FCSTD DOCUMENT  (FreeCAD 0.15R4671 (Git))
Label: YCarrageBottom_II
License: All rights reserved
LicenseURL: http://en.wikipedia.org/wiki/All_rights_reserved
objects: Sketcher::SketchObject×21, PartDesign::Pocket×17, Mesh::Feature×15, Part::Feature×8, PartDesign::Fillet×5, PartDesign::Pad×4, PartDesign::Chamfer×2
note: 78 computed .brp shape members not serialized (recipe doc carries the construction recipe); baked Part::Feature solids carry a one-line shape summary decoded from their .brp

FEATURE [Part::Feature] Part__Feature  label="YCarrage"
  shape: bbox 35 x 59 x 36 mm, 127 faces (baked)
FEATURE [Sketcher::SketchObject] Sketch
  Placement = pos=(0,0,-14) rot=(0,0,1;0rad)
  sketch-geometry (4):
    g0: LineSegment StartX=60 StartY=17 StartZ=0 EndX=22 EndY=17 EndZ=0
    g1: LineSegment StartX=22 StartY=17 StartZ=0 EndX=22 EndY=-42 EndZ=0
    g2: LineSegment StartX=22 StartY=-42 StartZ=0 EndX=60 EndY=-42 EndZ=0
    g3: LineSegment StartX=60 StartY=-42 StartZ=0 EndX=60 EndY=17 EndZ=0
  constraints (8):
    c: Coincident(g0,g1)
    c: Coincident(g1,g2)
    c: Coincident(g2,g3)
    c: Coincident(g3,g0)
    c: Horizontal(g0)
    c: Horizontal(g2)
    c: Vertical(g1)
    c: Vertical(g3)
FEATURE [PartDesign::Pad] Pad
  Length = 36
  Length2 = 100
  Placement = pos=(0,0,-14) rot=(0,0,1;0rad)
  Sketch = -> Sketch
  Type = 0
FEATURE [Sketcher::SketchObject] Sketch001
  Placement = pos=(0,0,22) rot=(0,0,1;0rad)
  Support = -> Pad [Face6]
  sketch-geometry (10):
    g0: LineSegment StartX=62 StartY=17 StartZ=0 EndX=58 EndY=17 EndZ=0
    g1: LineSegment StartX=58 StartY=17 StartZ=0 EndX=45 EndY=6 EndZ=0
    g2: LineSegment StartX=45 StartY=6 StartZ=0 EndX=45 EndY=-31 EndZ=0
    g3: LineSegment StartX=45 StartY=-31 StartZ=0 EndX=58 EndY=-42 EndZ=0
    g4: LineSegment StartX=58 StartY=-42 StartZ=0 EndX=61 EndY=-42 EndZ=0
    g5: LineSegment StartX=61 StartY=-42 StartZ=0 EndX=61 EndY=-44 EndZ=0
    g6: LineSegment StartX=61 StartY=-44 StartZ=0 EndX=20 EndY=-44 EndZ=0
    g7: LineSegment StartX=20 StartY=-44 StartZ=0 EndX=20 EndY=19 EndZ=0
    g8: LineSegment StartX=20 StartY=19 StartZ=0 EndX=62 EndY=19 EndZ=0
    g9: LineSegment StartX=62 StartY=19 StartZ=0 EndX=62 EndY=17 EndZ=0
  constraints (18):
    c: Horizontal(g0)
    c: Coincident(g0,g1)
    c: Coincident(g1,g2)
    c: Vertical(g2)
    c: Coincident(g2,g3)
    c: Coincident(g3,g4)
    c: Horizontal(g4)
    c: Coincident(g4,g5)
    c: Vertical(g5)
    c: Coincident(g5,g6)
    c: Horizontal(g6)
    c: Coincident(g6,g7)
    c: Vertical(g7)
    c: Coincident(g7,g8)
    c: Horizontal(g8)
    c: Coincident(g8,g9)
    c: Vertical(g9)
    c: Coincident(g0,g9)
FEATURE [PartDesign::Pocket] Pocket
  Length = 13
  Placement = pos=(0,0,-14) rot=(0,0,1;0rad)
  Sketch = -> Sketch001
  Type = 0
FEATURE [Sketcher::SketchObject] Sketch002
  Placement = pos=(0,-42,-14) rot=(1,0,0;1.5708rad)
  Support = -> Pocket [Face10]
  sketch-geometry (1):
    g0: Circle CenterX=36 CenterY=10.5 CenterZ=0 NormalX=0 NormalY=0 NormalZ=1 Radius=7.75
  constraints (1):
    c: Radius(g0) = 7.75
FEATURE [PartDesign::Pocket] Pocket001
  Length = 26.75
  Placement = pos=(0,0,-14) rot=(0,0,1;0rad)
  Sketch = -> Sketch002
  Type = 0
FEATURE [Sketcher::SketchObject] Sketch003
  Placement = pos=(0,17,-14) rot=(0,0.707107,0.707107;3.14159rad)
  Support = -> Pocket001 [Face2]
  sketch-geometry (1):
    g0: Circle CenterX=-36 CenterY=10.5 CenterZ=0 NormalX=0 NormalY=0 NormalZ=1 Radius=7.75
  constraints (1):
    c: Radius(g0) = 7.75
FEATURE [PartDesign::Pocket] Pocket002
  Length = 26.75
  Placement = pos=(0,0,-14) rot=(0,0,1;0rad)
  Sketch = -> Sketch003
  Type = 0
FEATURE [Sketcher::SketchObject] Sketch004
  Placement = pos=(0,-42,-14) rot=(1,0,0;1.5708rad)
  Support = -> Pocket002 [Face4]
  sketch-geometry (4):
    g0: LineSegment StartX=28 StartY=18.5 StartZ=0 EndX=44.5 EndY=18.5 EndZ=0
    g1: LineSegment StartX=44.5 StartY=18.5 StartZ=0 EndX=44.5 EndY=2.5 EndZ=0
    g2: LineSegment StartX=44.5 StartY=2.5 StartZ=0 EndX=28 EndY=2.5 EndZ=0
    g3: LineSegment StartX=28 StartY=2.5 StartZ=0 EndX=28 EndY=18.5 EndZ=0
  constraints (8):
    c: Coincident(g0,g1)
    c: Coincident(g1,g2)
    c: Coincident(g2,g3)
    c: Coincident(g3,g0)
    c: Horizontal(g0)
    c: Horizontal(g2)
    c: Vertical(g1)
    c: Vertical(g3)
FEATURE [PartDesign::Pad] Pad001
  Length = 1.25
  Length2 = 100
  Placement = pos=(0,0,-14) rot=(0,0,1;0rad)
  Reversed = true
  Sketch = -> Sketch004
  Type = 0
FEATURE [Sketcher::SketchObject] Sketch005
  Placement = pos=(0,17,-14) rot=(0,0.707107,0.707107;3.14159rad)
  Support = -> Pad001 [Face2]
  sketch-geometry (4):
    g0: LineSegment StartX=-44.6266 StartY=19 StartZ=0 EndX=-27.8702 EndY=19 EndZ=0
    g1: LineSegment StartX=-27.8702 StartY=19 StartZ=0 EndX=-27.8702 EndY=2.37723 EndZ=0
    g2: LineSegment StartX=-27.8702 StartY=2.37723 StartZ=0 EndX=-44.6266 EndY=2.37723 EndZ=0
    g3: LineSegment StartX=-44.6266 StartY=2.37723 StartZ=0 EndX=-44.6266 EndY=19 EndZ=0
  constraints (8):
    c: Coincident(g0,g1)
    c: Coincident(g1,g2)
    c: Coincident(g2,g3)
    c: Coincident(g3,g0)
    c: Horizontal(g0)
    c: Horizontal(g2)
    c: Vertical(g1)
    c: Vertical(g3)
FEATURE [PartDesign::Pad] Pad002
  Length = 1.25
  Length2 = 100
  Placement = pos=(0,0,-14) rot=(0,0,1;0rad)
  Reversed = true
  Sketch = -> Sketch005
  Type = 0
FEATURE [Part::Feature] Pad002001  label="Pad003"
  shape: bbox 38 x 59 x 36 mm, 16 faces (baked)
FEATURE [Sketcher::SketchObject] Sketch006
  Placement = pos=(0,17,0) rot=(0,0.707107,0.707107;3.14159rad)
  Support = -> Pad002001 [Face10]
  sketch-geometry (1):
    g0: Circle CenterX=-36 CenterY=-3.5 CenterZ=0 NormalX=0 NormalY=0 NormalZ=1 Radius=6
  constraints (1):
    c: Radius(g0) = 6
FEATURE [PartDesign::Pocket] Pocket003
  Length = 5
  Sketch = -> Sketch006
  Type = 1
FEATURE [Mesh::Feature] _mmRod_x100mm  label="8mmRod_x100mm001"
  Placement = pos=(45,7.5,1.5) rot=(0,0,1;1.5708rad)
FEATURE [Mesh::Feature] _mmRod_x100mm001  label="8mmRod_x100mm002"
  Placement = pos=(45,-32.5,1.5) rot=(0,0,1;1.5708rad)
FEATURE [Part::Feature] Part__Feature001  label="T5_Pulley"
  Placement = pos=(36,176,-4) rot=(0,0,1;0rad)
  shape: bbox 16 x 16 x 14.8 mm, 116 faces (baked)
FEATURE [Part::Feature] Part__Feature002  label="NEMA17"
  Placement = pos=(36,176,2) rot=(0,0,1;0rad)
  shape: bbox 42.3 x 42.3 x 68 mm, 275 faces (baked)
FEATURE [Part::Feature] LM8UU_8mm_Linear_Bearing
  Placement = pos=(36,-9,-3.5) rot=(0,0,1;1.5708rad)
  shape: bbox 15 x 24 x 15 mm, 34 faces (baked)
FEATURE [Mesh::Feature] _x10x4_FlangedBearing  label="5x10x4_FlangedBearing_BOTTOM"
  Placement = pos=(49,-6,16) rot=(-1,0,0;1.5708rad)
FEATURE [Mesh::Feature] _x10x4_FlangedBearing001  label="5x10x4_FlangedBearing_TOP"
  Placement = pos=(49,-6,12) rot=(1,0,0;1.5708rad)
FEATURE [Mesh::Feature] _x10x4_FlangedBearing002  label="5x10x4_FlangedBearing_BOTTOM001"
  Placement = pos=(49,-19,16) rot=(-1,0,0;1.5708rad)
FEATURE [Mesh::Feature] _x10x4_FlangedBearing003  label="5x10x4_FlangedBearing_TOP001"
  Placement = pos=(49,-19,12) rot=(1,0,0;1.5708rad)
FEATURE [Part::Feature] LM8UU_8mm_Linear_Bearing001
  Placement = pos=(36,-40,-3.5) rot=(0,0,1;1.5708rad)
  shape: bbox 15 x 24 x 15 mm, 34 faces (baked)
FEATURE [Mesh::Feature] HexNutStyle1_M002
  Placement = pos=(55.3,-11.85,-128.5) rot=(0,0,1;0.523599rad)
FEATURE [Mesh::Feature] HexNutStyle1_M003
  Placement = pos=(55.3,39.15,-128.5) rot=(0,0,1;0.523599rad)
FEATURE [Mesh::Feature] HexNutStyle1_M004
  Placement = pos=(55.3,13.65,-128.5) rot=(0,0,1;0.523599rad)
FEATURE [Sketcher::SketchObject] Sketch007
  Placement = pos=(45,0,0) rot=(0.57735,-0.57735,-0.57735;2.0944rad)
  Support = -> Pocket003 [Face12]
  sketch-geometry (4):
    g0: LineSegment StartX=-1.75 StartY=18.25 StartZ=0 EndX=26.75 EndY=18.25 EndZ=0
    g1: LineSegment StartX=26.75 StartY=18.25 StartZ=0 EndX=26.75 EndY=9.75 EndZ=0
    g2: LineSegment StartX=26.75 StartY=9.75 StartZ=0 EndX=-1.75 EndY=9.75 EndZ=0
    g3: LineSegment StartX=-1.75 StartY=9.75 StartZ=0 EndX=-1.75 EndY=18.25 EndZ=0
  constraints (8):
    c: Coincident(g0,g1)
    c: Coincident(g1,g2)
    c: Coincident(g2,g3)
    c: Coincident(g3,g0)
    c: Horizontal(g0)
    c: Horizontal(g2)
    c: Vertical(g1)
    c: Vertical(g3)
FEATURE [PartDesign::Pocket] Pocket004
  Length = 11
  Sketch = -> Sketch007
  Type = 0
FEATURE [Sketcher::SketchObject] Sketch008
  Placement = pos=(60,0,0) rot=(0.57735,0.57735,0.57735;2.0944rad)
  Support = -> Pocket004 [Face5]
  sketch-geometry (4):
    g0: LineSegment StartX=-15 StartY=18.25 StartZ=0 EndX=-10 EndY=18.25 EndZ=0
    g1: LineSegment StartX=-10 StartY=18.25 StartZ=0 EndX=-10 EndY=9.75 EndZ=0
    g2: LineSegment StartX=-10 StartY=9.75 StartZ=0 EndX=-15 EndY=9.75 EndZ=0
    g3: LineSegment StartX=-15 StartY=9.75 StartZ=0 EndX=-15 EndY=18.25 EndZ=0
  constraints (8):
    c: Coincident(g0,g1)
    c: Coincident(g1,g2)
    c: Coincident(g2,g3)
    c: Coincident(g3,g0)
    c: Horizontal(g0)
    c: Horizontal(g2)
    c: Vertical(g1)
    c: Vertical(g3)
FEATURE [PartDesign::Pocket] Pocket005
  Length = 5
  Sketch = -> Sketch008
  Type = 1
FEATURE [Sketcher::SketchObject] Sketch009
  Placement = pos=(0,0,22) rot=(0,0,1;0rad)
  Support = -> Pocket005 [Face7]
  sketch-geometry (2):
    g0: Circle CenterX=49 CenterY=-6 CenterZ=0 NormalX=0 NormalY=0 NormalZ=1 Radius=1.8
    g1: Circle CenterX=49 CenterY=-19 CenterZ=0 NormalX=0 NormalY=0 NormalZ=1 Radius=1.8
  constraints (2):
    c: Radius(g1) = 1.8
    c: Equal(g1,g0)
FEATURE [PartDesign::Pocket] Pocket006
  Length = 30
  Sketch = -> Sketch009
  Type = 0
FEATURE [Sketcher::SketchObject] Sketch010
  Placement = pos=(0,0,-14) rot=(1,0,0;3.14159rad)
  Support = -> Pocket006 [Face1]
  sketch-geometry (2):
    g0: Circle CenterX=49 CenterY=19 CenterZ=0 NormalX=0 NormalY=0 NormalZ=1 Radius=1
    g1: Circle CenterX=49 CenterY=6 CenterZ=0 NormalX=0 NormalY=0 NormalZ=1 Radius=1
  constraints (2):
    c: Radius(g0) = 1
    c: Equal(g0,g1)
FEATURE [PartDesign::Pocket] Pocket007
  Length = 5
  Sketch = -> Sketch010
  Type = 1
FEATURE [PartDesign::Chamfer] Chamfer
  Base = -> Pocket007 [Edge65,Edge54]
  Size = 3.5
FEATURE [Mesh::Feature] HexNutStyle1_M
  Placement = pos=(25.3,-1.84,-117) rot=(0,0,1;0.523599rad)
FEATURE [Mesh::Feature] SocketHeadCapScrew_M3x  label="SocketHeadCapScrew_M3x8"
  Placement = pos=(16.1,-18.09,109) rot=(0,1,0;3.14159rad)
FEATURE [Mesh::Feature] HexNutStyle1_M005
  Placement = pos=(25.3,29.16,-117) rot=(0,0,1;0.523599rad)
FEATURE [Mesh::Feature] SocketHeadCapScrew_M3x001  label="SocketHeadCapScrew_M3x009"
  Placement = pos=(16.1,12.91,109) rot=(0,1,0;3.14159rad)
FEATURE [Mesh::Feature] HexNutStyle1_M006
  Placement = pos=(49,14,-117) rot=(0,0,1;0.523599rad)
FEATURE [Mesh::Feature] SocketHeadCapScrew_M3x002  label="SocketHeadCapScrew_M3x010"
  Placement = pos=(39.8,-2.25,109) rot=(0,1,0;3.14159rad)
FEATURE [Sketcher::SketchObject] Sketch012
  Placement = pos=(0,0,9) rot=(0,0,1;0rad)
  Support = -> Chamfer [Face20]
  sketch-geometry (8):
    g0: ArcOfCircle CenterX=24 CenterY=-28 CenterZ=0 NormalX=0 NormalY=0 NormalZ=1 Radius=5 StartAngle=1.5708 EndAngle=4.71239
    g1: LineSegment StartX=24 StartY=-33 StartZ=0 EndX=25 EndY=-33 EndZ=0
    g2: LineSegment StartX=25 StartY=-33 StartZ=0 EndX=25 EndY=-23 EndZ=0
    g3: LineSegment StartX=25 StartY=-23 StartZ=0 EndX=24 EndY=-23 EndZ=0
    g4: ArcOfCircle CenterX=24 CenterY=3 CenterZ=0 NormalX=0 NormalY=0 NormalZ=1 Radius=5 StartAngle=1.5708 EndAngle=4.71239
    g5: LineSegment StartX=24 StartY=-2 StartZ=0 EndX=25 EndY=-2 EndZ=0
    g6: LineSegment StartX=25 StartY=-2 StartZ=0 EndX=25 EndY=8 EndZ=0
    g7: LineSegment StartX=25 StartY=8 StartZ=0 EndX=24 EndY=8 EndZ=0
  constraints (14):
    c: Tangent(g0,g1) = -1.5708
    c: Coincident(g1,g2)
    c: Vertical(g2)
    c: Coincident(g2,g3)
    c: Coincident(g3,g0)
    c: Horizontal(g3)
    c: Radius(g0) = 5
    c: Radius(g4) = 5
    c: Tangent(g4,g5) = -1.5708
    c: Coincident(g5,g6)
    c: Vertical(g6)
    c: Coincident(g6,g7)
    c: Coincident(g7,g4)
    c: Horizontal(g7)
FEATURE [PartDesign::Pad] Pad002002
  Length = 23
  Length2 = 100
  Reversed = true
  Sketch = -> Sketch012
  Type = 0
FEATURE [Sketcher::SketchObject] Sketch013
  Placement = pos=(0,0,9) rot=(0,0,1;0rad)
  Support = -> Pad002002 [Face41]
  sketch-geometry (2):
    g0: Circle CenterX=24 CenterY=3 CenterZ=0 NormalX=0 NormalY=0 NormalZ=1 Radius=1.8
    g1: Circle CenterX=24 CenterY=-28 CenterZ=0 NormalX=0 NormalY=0 NormalZ=1 Radius=1.8
  constraints (2):
    c: Radius(g1) = 1.8
    c: Equal(g1,g0)
FEATURE [PartDesign::Pocket] Pocket008
  Length = 5
  Sketch = -> Sketch013
  Type = 1
FEATURE [Sketcher::SketchObject] Sketch014
  Placement = pos=(0,0,-14) rot=(1,0,0;3.14159rad)
  Support = -> Pocket008 [Face16]
  sketch-geometry (2):
    g0: Circle CenterX=24 CenterY=28 CenterZ=0 NormalX=0 NormalY=0 NormalZ=1 Radius=3.5
    g1: Circle CenterX=24 CenterY=-3 CenterZ=0 NormalX=0 NormalY=0 NormalZ=1 Radius=3.5
  constraints (2):
    c: Radius(g0) = 3.5
    c: Equal(g0,g1)
FEATURE [PartDesign::Pocket] Pocket009
  Length = 8.5
  Sketch = -> Sketch014
  Type = 0
FEATURE [Sketcher::SketchObject] Sketch015
  Placement = pos=(22,0,0) rot=(0.57735,-0.57735,-0.57735;2.0944rad)
  Support = -> Pocket009 [Face28]
  sketch-geometry (8):
    g0: LineSegment StartX=-6 StartY=2.25 StartZ=0 EndX=0 EndY=2.25 EndZ=0
    g1: LineSegment StartX=0 StartY=2.25 StartZ=0 EndX=0 EndY=-0.5 EndZ=0
    g2: LineSegment StartX=0 StartY=-0.5 StartZ=0 EndX=-6 EndY=-0.5 EndZ=0
    g3: LineSegment StartX=-6 StartY=-0.5 StartZ=0 EndX=-6 EndY=2.25 EndZ=0
    g4: LineSegment StartX=25 StartY=2.25 StartZ=0 EndX=31 EndY=2.25 EndZ=0
    g5: LineSegment StartX=31 StartY=2.25 StartZ=0 EndX=31 EndY=-0.5 EndZ=0
    g6: LineSegment StartX=31 StartY=-0.5 StartZ=0 EndX=25 EndY=-0.5 EndZ=0
    g7: LineSegment StartX=25 StartY=-0.5 StartZ=0 EndX=25 EndY=2.25 EndZ=0
  constraints (17):
    c: Coincident(g0,g1)
    c: Coincident(g1,g2)
    c: Coincident(g2,g3)
    c: Coincident(g3,g0)
    c: Horizontal(g0)
    c: Horizontal(g2)
    c: Vertical(g1)
    c: Vertical(g3)
    c: PointOnObject(g1,g-2)
    c: Coincident(g4,g5)
    c: Coincident(g5,g6)
    c: Coincident(g6,g7)
    c: Coincident(g7,g4)
    c: Horizontal(g4)
    c: Horizontal(g6)
    c: Vertical(g5)
    c: Vertical(g7)
FEATURE [PartDesign::Pocket] Pocket010
  Length = 11.5
  Midplane = true
  Sketch = -> Sketch015
  Type = 0
FEATURE [Sketcher::SketchObject] Sketch016
  Placement = pos=(60,0,0) rot=(0.57735,0.57735,0.57735;2.0944rad)
  Support = -> Pocket010 [Face4]
  sketch-geometry (4):
    g0: LineSegment StartX=-15 StartY=2.25 StartZ=0 EndX=-9.25 EndY=2.25 EndZ=0
    g1: LineSegment StartX=-9.25 StartY=2.25 StartZ=0 EndX=-9.25 EndY=-0.5 EndZ=0
    g2: LineSegment StartX=-9.25 StartY=-0.5 StartZ=0 EndX=-15 EndY=-0.5 EndZ=0
    g3: LineSegment StartX=-15 StartY=-0.5 StartZ=0 EndX=-15 EndY=2.25 EndZ=0
  constraints (8):
    c: Coincident(g0,g1)
    c: Coincident(g1,g2)
    c: Coincident(g2,g3)
    c: Coincident(g3,g0)
    c: Horizontal(g0)
    c: Horizontal(g2)
    c: Vertical(g1)
    c: Vertical(g3)
FEATURE [PartDesign::Pocket] Pocket011
  Length = 16
  Sketch = -> Sketch016
  Type = 0
FEATURE [Sketcher::SketchObject] Sketch017
  Placement = pos=(0,0,-14) rot=(1,0,0;3.14159rad)
  Support = -> Pocket011 [Face16]
  sketch-geometry (1):
    g0: Circle CenterX=47.6923 CenterY=12.121 CenterZ=0 NormalX=0 NormalY=0 NormalZ=1 Radius=1.8
  constraints (1):
    c: Radius(g0) = 1.8
FEATURE [PartDesign::Pocket] Pocket012
  Length = 18
  Sketch = -> Sketch017
  Type = 0
FEATURE [Sketcher::SketchObject] Sketch018
  Placement = pos=(0,0,-14) rot=(1,0,0;3.14159rad)
  Support = -> Pocket012 [Face16]
  sketch-geometry (1):
    g0: Circle CenterX=47.6917 CenterY=12.1202 CenterZ=0 NormalX=0 NormalY=0 NormalZ=1 Radius=3.5
  constraints (1):
    c: Radius(g0) = 3.5
FEATURE [PartDesign::Pocket] Pocket013
  Length = 8.5
  Sketch = -> Sketch018
  Type = 0
FEATURE [Sketcher::SketchObject] Sketch019
  Placement = pos=(60,0,0) rot=(0.57735,0.57735,0.57735;2.0944rad)
  Support = -> Pocket013 [Face4]
  sketch-geometry (2):
    g0: Circle CenterX=-32.5 CenterY=1.5 CenterZ=0 NormalX=0 NormalY=0 NormalZ=1 Radius=4.2
    g1: Circle CenterX=7.5 CenterY=1.5 CenterZ=0 NormalX=0 NormalY=0 NormalZ=1 Radius=4.2
  constraints (2):
    c: Radius(g1) = 4.2
    c: Equal(g1,g0)
FEATURE [PartDesign::Pocket] Pocket014
  Length = 15
  Sketch = -> Sketch019
  Type = 0
FEATURE [Part::Feature] Pocket015
  shape: bbox 41 x 59 x 36 mm, 73 faces (baked)
FEATURE [PartDesign::Chamfer] Chamfer001
  Base = -> Pocket015 [Edge76,Edge60]
  Size = 4
FEATURE [PartDesign::Fillet] Fillet
  Base = -> Chamfer001 [Edge59,Edge62,Edge63,Edge64,Edge69,Edge70,Edge23,Edge2]
  Radius = 2
FEATURE [PartDesign::Fillet] Fillet001
  Base = -> Fillet [Edge151,Edge66]
  Radius = 2
FEATURE [PartDesign::Fillet] Fillet002
  Base = -> Fillet001 [Edge53,Edge27]
  Radius = 2
FEATURE [PartDesign::Fillet] Fillet003
  Base = -> Fillet002 [Edge26,Edge96]
  Radius = 1
FEATURE [PartDesign::Fillet] Fillet004
  Base = -> Fillet003 [Edge48]
  Radius = 1
FEATURE [Part::Feature] Fillet005
  shape: bbox 41.33 x 59.33 x 36 mm, 130 faces (baked)
FEATURE [Sketcher::SketchObject] Sketch020
  Placement = pos=(0,-42,0) rot=(1,0,0;1.5708rad)
  Support = -> Fillet005 [Face50]
  sketch-geometry (6):
    g0: LineSegment StartX=16.714 StartY=-3.5 StartZ=0 EndX=53.5 EndY=-3.5 EndZ=0
    g1: LineSegment StartX=53.5 StartY=-3.5 StartZ=0 EndX=53.5 EndY=-15 EndZ=0
    g2: LineSegment StartX=53.5 StartY=-15 StartZ=0 EndX=63.1788 EndY=-15 EndZ=0
    g3: LineSegment StartX=63.1788 StartY=-15 StartZ=0 EndX=63.1788 EndY=24.1424 EndZ=0
    g4: LineSegment StartX=63.1788 StartY=24.1424 StartZ=0 EndX=16.714 EndY=24.1424 EndZ=0
    g5: LineSegment StartX=16.714 StartY=24.1424 StartZ=0 EndX=16.714 EndY=-3.5 EndZ=0
  constraints (12):
    c: Coincident(g0,g1)
    c: Horizontal(g0)
    c: Vertical(g1)
    c: Coincident(g1,g2)
    c: Horizontal(g2)
    c: Coincident(g2,g3)
    c: Vertical(g3)
    c: Coincident(g3,g4)
    c: Horizontal(g4)
    c: Coincident(g4,g5)
    c: Coincident(g5,g0)
    c: Vertical(g5)
FEATURE [PartDesign::Pocket] Pocket016  label="YCarrageBottom"
  Length = 5
  Sketch = -> Sketch020
  Type = 1
FEATURE [Sketcher::SketchObject] Sketch021
  Placement = pos=(0,-42,0) rot=(1,0,0;1.5708rad)
  Support = -> Pocket016 [Face8]
  sketch-geometry (6):
    g0: LineSegment StartX=53.75 StartY=-14.25 StartZ=0 EndX=53.25 EndY=-14.25 EndZ=0
    g1: LineSegment StartX=53.25 StartY=-14.25 StartZ=0 EndX=53.25 EndY=-3.75 EndZ=0
    g2: LineSegment StartX=53.25 StartY=-3.75 StartZ=0 EndX=18.75 EndY=-3.75 EndZ=0
    g3: LineSegment StartX=18.75 StartY=-3.75 StartZ=0 EndX=18.75 EndY=-3.25 EndZ=0
    g4: LineSegment StartX=18.75 StartY=-3.25 StartZ=0 EndX=53.75 EndY=-3.25 EndZ=0
    g5: LineSegment StartX=53.75 StartY=-3.25 StartZ=0 EndX=53.75 EndY=-14.25 EndZ=0
  constraints (6):
    c: Coincident(g0,g1)
    c: Coincident(g1,g2)
    c: Coincident(g2,g3)
    c: Coincident(g3,g4)
    c: Coincident(g4,g5)
    c: Coincident(g5,g0)
FEATURE [PartDesign::Pocket] Pocket017  label="YCarrageBottom_trimed"
  Length = 5
  Sketch = -> Sketch021
  Type = 1
